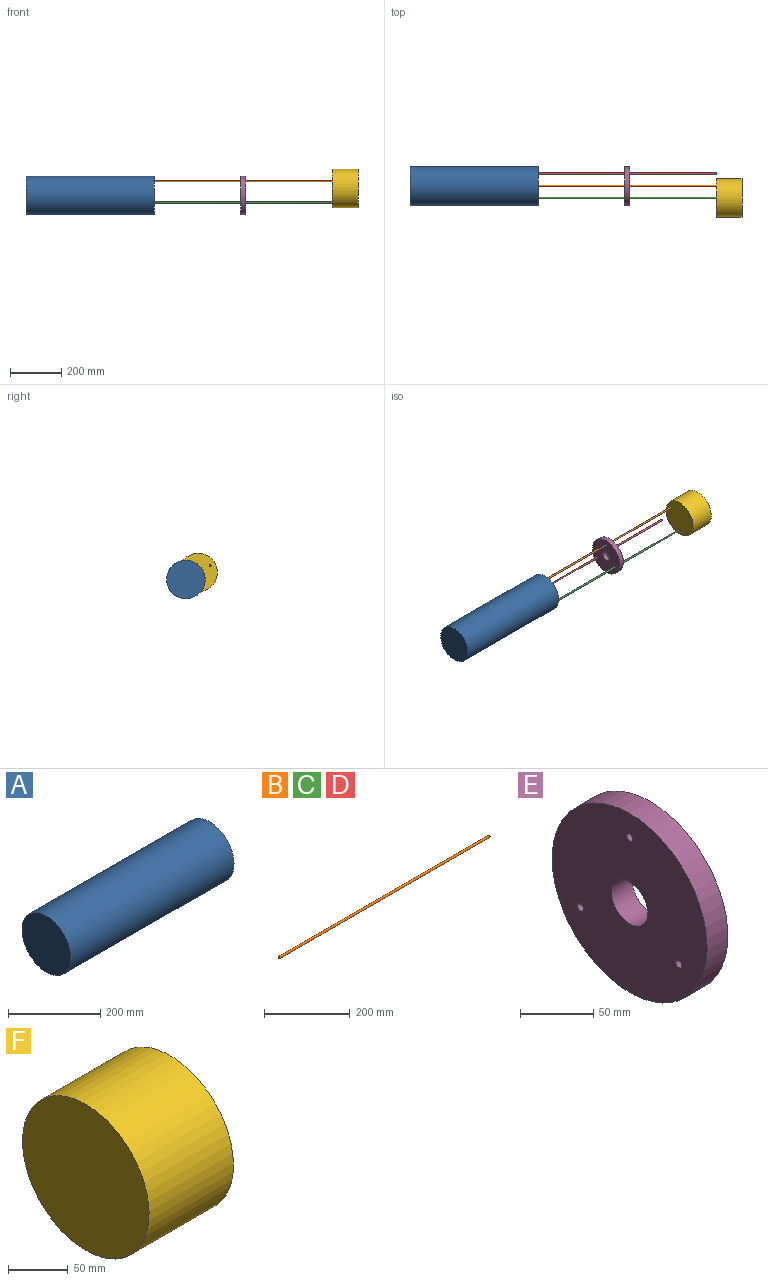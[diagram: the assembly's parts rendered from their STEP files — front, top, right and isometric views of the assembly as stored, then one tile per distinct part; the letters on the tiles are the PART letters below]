
ASSEMBLY  parts=6 mates=5
PART A: 11 faces, bbox 500x150x150 mm
  f0: cylinder r=75mm len=500mm, axis (1,0,0), area 235619.4mm2, adj f1,f4
  f1: plane 150x150mm, normal (1,0,0), area 16624.5mm2, adj f0,f2,f5,f7,f9
  f2: cylinder r=17.5mm len=70mm, axis (1,0,0), area 7696.9mm2, adj f1,f3
  f3: plane 35x35mm, normal (1,0,0), area 962.1mm2, adj f2
  f4: plane 150x150mm, normal (-1,0,0), area 17671.5mm2, adj f0
  f5: cylinder r=3mm len=25mm, axis (1,0,0), area 471.2mm2, adj f1,f6
  f6: plane 6x6mm, normal (1,0,0), area 28.3mm2, adj f5
  f7: cylinder r=3mm len=25mm, axis (1,0,0), area 471.2mm2, adj f1,f8
  f8: plane 6x6mm, normal (1,0,0), area 28.3mm2, adj f7
  f9: cylinder r=3mm len=25mm, axis (1,0,0), area 471.2mm2, adj f1,f10
  f10: plane 6x6mm, normal (1,0,0), area 28.3mm2, adj f9
PART B: 3 faces, bbox 695x6x6 mm
  f0: plane 6x6mm, normal (1,0,0), area 28.3mm2, adj f2
  f1: plane 6x6mm, normal (-1,0,0), area 28.3mm2, adj f2
  f2: cylinder r=3mm len=695mm, axis (1,0,0), area 13100.4mm2, adj f0,f1
PART C: same geometry as B
PART D: same geometry as B
PART E: 7 faces, bbox 20x150x150 mm
  f0: plane 150x150mm, normal (-1,0,0), area 16624.5mm2, adj f1,f3,f4,f5,f6
  f1: cylinder r=75mm len=150mm, axis (-1,0,0), area 9424.8mm2, adj f0,f2
  f2: plane 150x150mm, normal (1,0,0), area 16624.5mm2, adj f1,f3,f4,f5,f6
  f3: cylinder r=17.5mm len=35mm, axis (-1,0,0), area 2199.1mm2, adj f0,f2
  f4: cylinder r=3mm len=20mm, axis (-1,0,0), area 377mm2, adj f0,f2
  f5: cylinder r=3mm len=20mm, axis (-1,0,0), area 377mm2, adj f0,f2
  f6: cylinder r=3mm len=20mm, axis (-1,0,0), area 377mm2, adj f0,f2
PART F: 9 faces, bbox 100x150x150 mm
  f0: plane 150x150mm, normal (1,0,0), area 17586.6mm2, adj f2,f3,f5,f7
  f1: plane 150x150mm, normal (-1,0,0), area 17671.5mm2, adj f2
  f2: cylinder r=75mm len=150mm, axis (1,0,0), area 47123.9mm2, adj f0,f1
  f3: cylinder r=3mm len=25mm, axis (1,0,0), area 471.2mm2, adj f0,f4
  f4: plane 6x6mm, normal (1,0,0), area 28.3mm2, adj f3
  f5: cylinder r=3mm len=25mm, axis (1,0,0), area 471.2mm2, adj f0,f6
  f6: plane 6x6mm, normal (1,0,0), area 28.3mm2, adj f5
  f7: cylinder r=3mm len=25mm, axis (1,0,0), area 471.2mm2, adj f0,f8
  f8: plane 6x6mm, normal (1,0,0), area 28.3mm2, adj f7
PLACE A t=(-695,0,110)mm
PLACE B rot(axis=(1,0,0),180deg) t=(0,0,165)mm
PLACE C rot(axis=(-1,0,0),90deg) t=(0,-47.63,82.5)mm
PLACE D t=(0,47.63,82.5)mm
PLACE E t=(-357.5,0,110)mm
PLACE F rot(axis=(0,1,0),180deg) t=(0,-47.63,137.5)mm
MATE revolute F.f3 <-> B.f2  axis (-1,0,0) through (0,0,165)mm
MATE fastened C.f2 <-> A.f7  axis (-1,0,0) through (-695,-47.63,82.5)mm
MATE fastened A.f5 <-> D.f2  axis (1,0,0) through (-695,47.63,82.5)mm
MATE cylindrical E.f4 <-> B.f2  axis (-1,0,0) through (-347.5,0,165)mm
MATE fastened B.f2 <-> A.f9  axis (1,0,0) through (-695,0,165)mm
